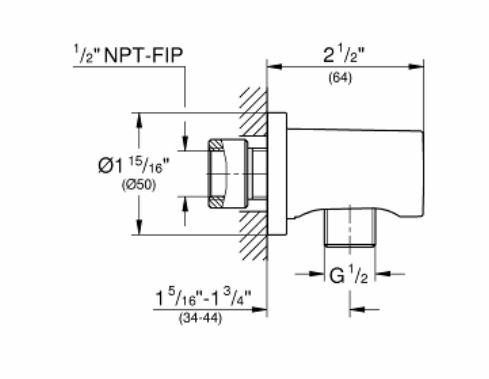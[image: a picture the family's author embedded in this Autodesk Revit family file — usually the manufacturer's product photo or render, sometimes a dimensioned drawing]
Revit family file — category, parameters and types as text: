
# Revit family: Commercial_Rainshower_System-GROHE-Cosmopolitan-29428_Series.rfazzz
name_source: partatom
category: Plumbing Fixtures
units: mm (PartAtom-declared; Revit-internal decimal feet)

## family parameters
Cut with Voids When Loaded = No
Host = Face
OmniClass Number = 23.45.05.14.17
OmniClass Title = Showers
Part Type = Normal
Room Calculation Point = No
Round Connector Dimension = Use Diameter
Shared = Yes

## types (2) — shared parameters
26 046- Tempesta® Cosmopolitan 100 handshower, 2 sprays, 1.75gpm = Yes
26 175- Tempasta® 250 showerhead, 1 spray, 1.75gpm = Yes
26 635- Rainshower™ wall union = Yes
27 521- Tempesta® Cosmopolitan 24” Shower Bar = Yes
28 417- RotaFlex Metal Longlife metallic hose = Yes
28 540- Rainshower™ 15” shower arm = Yes
29 434- Cosmopolitan Pressure Balance Valve Trim with 2-Way Diverter = Yes
35 117- GrohSafe™ 3.0 Pressure Balance Rough Valve with Integrated Diverter = Yes
ASME A112.18.1/CSA B125.1/ASSE 1016 = Yes
ASSE 1016 = Yes
Assembly Code = D2010710
CEC Compliant = Yes
CW Connection = Yes
CWFU = 3
CalGreen Compliant = Yes
Cold Water Connection Diameter = 1/2"
Connection Diameter = 1/2"
Default Elevation = 0"
Description = COSMOPOLITAN- Pressure Balance Rainshower Set
Double check valves = Included
EPA WaterSense® Certified = Yes
Flow Rate = Max. 1.75gpm (6.6L/min)
HW Connection = Yes
HWFU = 3
Height- Diverter = 48"
Height- Showerhead = 78"
Hot Water Connection Diameter = 1/2"
IAPMO Compliance = Massachusetts Plumbing Board Approved, Energy Policy Act of 1992, CSA B125.16
Installation Type = Wall Mounted
Manufacturer = GROHE
Price = Prices may vary. Please consult Manufacturer Representative for most up-to-date price list.
Tempered Water Connection = Yes
URL = https://www.grohe.us
Vent Connection = No
WFU = 4
Waste Connection = No

## per-type parameters (varying)
| type | Finish | Material |
| 29428000 | Metal-Grohe-000-StarLight Chrome | Metal-Grohe-000-StarLight Chrome |
| 29428EN0 | Metal-Grohe-EN0-Brushed Nickel Infinity Finish | Metal-Grohe-EN0-Brushed Nickel Infinity Finish |

note: column(s) folded — value = type name in every type: Model

## geometry (parser evidence)
native form markers: Sweep x15
no freeform markers — native parametric forms only
